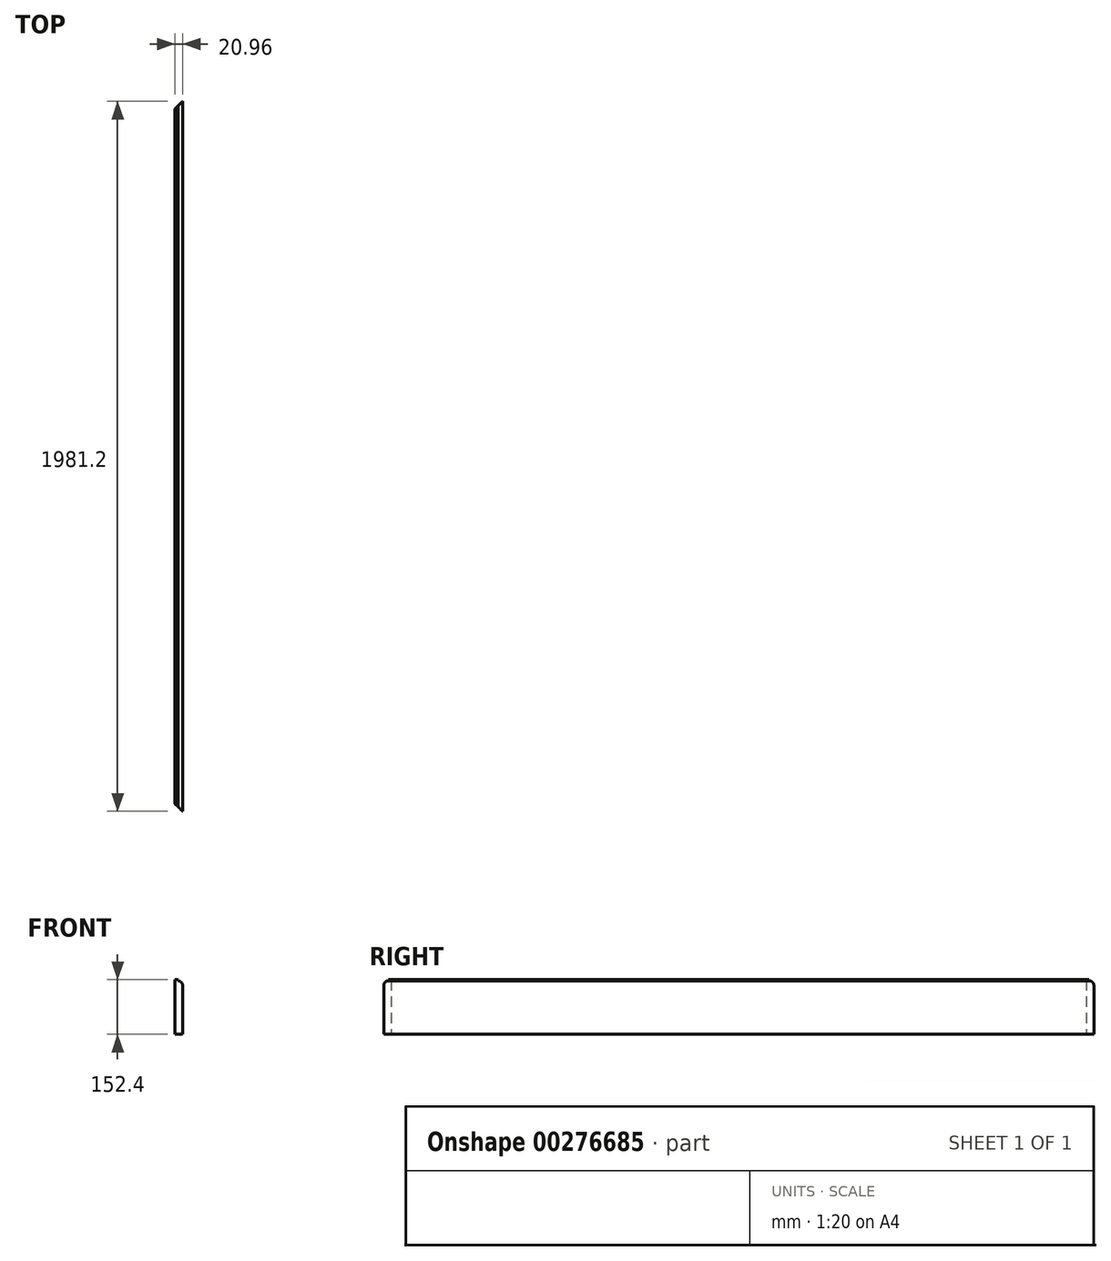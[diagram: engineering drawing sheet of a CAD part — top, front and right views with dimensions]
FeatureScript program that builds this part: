
annotation { "Feature Type Name" : "Feature", "Feature Type Description" : "" }
export const myFeature = defineFeature(function(context is Context, id is Id, definition is map)
    precondition{}
    {
        {
            var Q0;
            Q0=qCreatedBy(makeId("Front.planeOp"),FACE);
            var sketch = newSketch(context, id + "F0", { "sketchPlane" : qUnion([Q0])});
            skLineSegment(sketch, "E0.bottom", {"start": v(0, 0) * mm, "end": v(20.95, 0) * mm});
            skLineSegment(sketch, "E0.top", {"start": v(0, 152.4) * mm, "end": v(8, 152.4) * mm});
            skLineSegment(sketch, "E0.left", {"start": v(0, 0) * mm, "end": v(0, 152.4) * mm});
            skLineSegment(sketch, "E1", {"start": v(8, 152.4) * mm, "end": v(8, 149.22) * mm});
            skLineSegment(sketch, "E2", {"start": v(20.95, 136.53) * mm, "end": v(20.95, 0) * mm});
            skArc(sketch, "E3", {"start": v(20.95, 136.53) * mm, "mid": v(17.15, 145.6) * mm, "end": v(8, 149.22) * mm});
            skSolve(sketch);
        }
        {
            var Q0;
            Q0=makeQuery(id+"F0.imprint","IMPRINT",FACE,{"disambiguationData":[TD([[makeQuery(id+"F0.imprint","IMPRINT",EDGE,{"derivedFrom":sQuery(id+"F0.wireOp",EDGE,"E0.bottom")}),1.0]])]});
            extrude(context, id + "F1", {"entities" : qUnion([Q0]), "oppositeDirection" : true, "offsetDistance" : 25.4 * mm, "depth" : 1981.2 * mm});
        }
        {
            var Q0;
            Q0=makeQuery(id+"F1.opExtrude","SWEPT_FACE",FACE,{"disambiguationData":[OSD([sQuery(id+"F0.wireOp",EDGE,"E0.bottom")])]});
            var sketch = newSketch(context, id + "F2", { "sketchPlane" : qUnion([Q0])});
            skLineSegment(sketch, "E4", {"start": v(20.95, 0) * mm, "end": v(0, -20.95) * mm});
            skSolve(sketch);
        }
        {
            var Q0;
            {var subQ0=sQuery(id+"F2.wireOp",EDGE,"E4");Q0=makeQuery(id+"F2.imprint","IMPRINT",FACE,{"disambiguationData":[TD([[makeQuery(id+"F2.imprint","IMPRINT",EDGE,{"derivedFrom":subQ0}),-1.0]])]});}
            extrude(context, id + "F3", {"entities" : qUnion([Q0]), "operationType" : NewBodyOperationType.REMOVE, "oppositeDirection" : true, "depth" : 152.4 * mm});
        }
        {
            var Q0;
            Q0=makeQuery(id+"F1.opExtrude","SWEPT_FACE",FACE,{"disambiguationData":[OSD([sQuery(id+"F0.wireOp",EDGE,"E0.bottom")])]});
            var sketch = newSketch(context, id + "F4", { "sketchPlane" : qUnion([Q0])});
            skLineSegment(sketch, "E5", {"start": v(20.96, -1981.2) * mm, "end": v(0, -1960.25) * mm});
            skSolve(sketch);
        }
        {
            var Q0;
            {var subQ0=sQuery(id+"F4.wireOp",EDGE,"E5");Q0=makeQuery(id+"F4.imprint","IMPRINT",FACE,{"disambiguationData":[TD([[makeQuery(id+"F4.imprint","IMPRINT",EDGE,{"derivedFrom":subQ0}),1.0]])]});}
            extrude(context, id + "F5", {"entities" : qUnion([Q0]), "operationType" : NewBodyOperationType.REMOVE, "oppositeDirection" : true, "depth" : 152.4 * mm});
        }
    });
